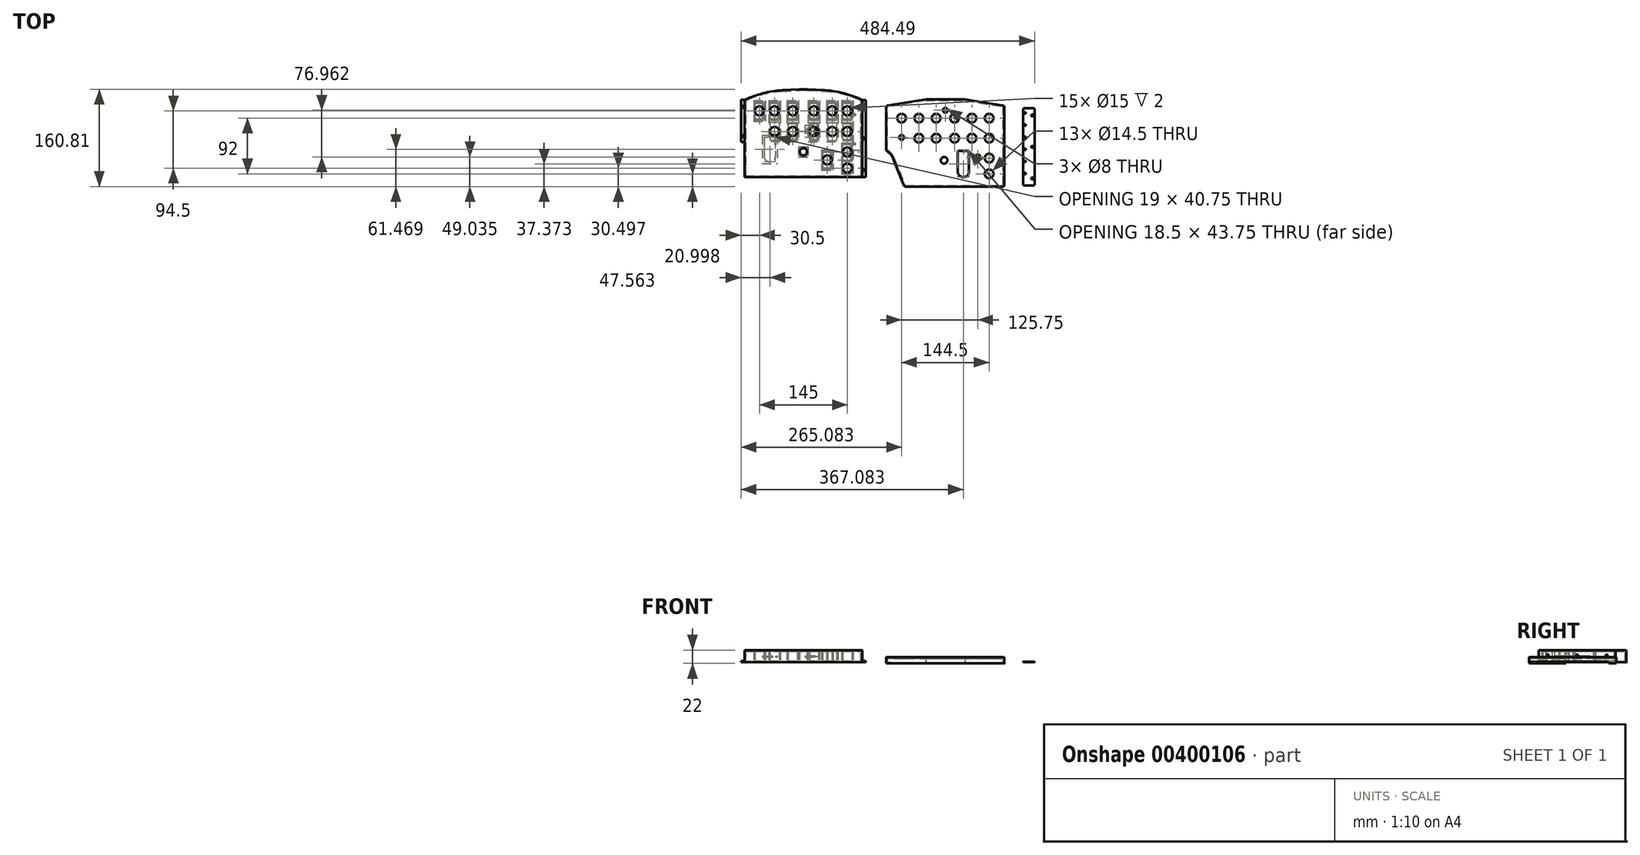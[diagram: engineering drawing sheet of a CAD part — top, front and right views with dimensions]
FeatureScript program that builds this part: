
annotation { "Feature Type Name" : "Feature", "Feature Type Description" : "" }
export const myFeature = defineFeature(function(context is Context, id is Id, definition is map)
    precondition{}
    {
        {
            var Q0;
            Q0=qCreatedBy(makeId("Top.planeOp"),FACE);
            var sketch = newSketch(context, id + "F0", { "sketchPlane" : qUnion([Q0])});
            skLineSegment(sketch, "E0.bottom", {"start": v(-74, 30.66) * mm, "end": v(-59, 30.66) * mm});
            skLineSegment(sketch, "E0.top", {"start": v(-74, 0.66) * mm, "end": v(-59, 0.66) * mm});
            skLineSegment(sketch, "E0.left", {"start": v(-74, 30.66) * mm, "end": v(-74, 0.66) * mm});
            skLineSegment(sketch, "E0.right", {"start": v(-59, 30.66) * mm, "end": v(-59, 0.66) * mm});
            skLineSegment(sketch, "E1.bottom", {"start": v(-49, 30.66) * mm, "end": v(-34, 30.66) * mm});
            skLineSegment(sketch, "E1.top", {"start": v(-49, 0.66) * mm, "end": v(-34, 0.66) * mm});
            skLineSegment(sketch, "E1.left", {"start": v(-49, 30.66) * mm, "end": v(-49, 0.66) * mm});
            skLineSegment(sketch, "E1.right", {"start": v(-34, 30.66) * mm, "end": v(-34, 0.66) * mm});
            skLineSegment(sketch, "E2.bottom", {"start": v(-19, 30.66) * mm, "end": v(-4, 30.66) * mm});
            skLineSegment(sketch, "E2.top", {"start": v(-19, 0.66) * mm, "end": v(-4, 0.66) * mm});
            skLineSegment(sketch, "E2.left", {"start": v(-19, 30.66) * mm, "end": v(-19, 0.66) * mm});
            skLineSegment(sketch, "E2.right", {"start": v(-4, 30.66) * mm, "end": v(-4, 0.66) * mm});
            skLineSegment(sketch, "E3.bottom", {"start": v(16, 30.66) * mm, "end": v(31, 30.66) * mm});
            skLineSegment(sketch, "E3.top", {"start": v(16, 0.66) * mm, "end": v(31, 0.66) * mm});
            skLineSegment(sketch, "E3.left", {"start": v(16, 30.66) * mm, "end": v(16, 0.66) * mm});
            skLineSegment(sketch, "E3.right", {"start": v(31, 30.66) * mm, "end": v(31, 0.66) * mm});
            skLineSegment(sketch, "E4.bottom", {"start": v(46, 30.66) * mm, "end": v(61, 30.66) * mm});
            skLineSegment(sketch, "E4.top", {"start": v(46, 0.66) * mm, "end": v(61, 0.66) * mm});
            skLineSegment(sketch, "E4.left", {"start": v(46, 30.66) * mm, "end": v(46, 0.66) * mm});
            skLineSegment(sketch, "E4.right", {"start": v(61, 30.66) * mm, "end": v(61, 0.66) * mm});
            skLineSegment(sketch, "E5.bottom", {"start": v(71, 30.66) * mm, "end": v(86, 30.66) * mm});
            skLineSegment(sketch, "E5.top", {"start": v(71, 0.66) * mm, "end": v(86, 0.66) * mm});
            skLineSegment(sketch, "E5.left", {"start": v(71, 30.66) * mm, "end": v(71, 0.66) * mm});
            skLineSegment(sketch, "E5.right", {"start": v(86, 30.66) * mm, "end": v(86, 0.66) * mm});
            skLineSegment(sketch, "E6.bottom", {"start": v(-19, -3.34) * mm, "end": v(-4, -3.34) * mm});
            skLineSegment(sketch, "E6.top", {"start": v(-19, -33.34) * mm, "end": v(-4, -33.34) * mm});
            skLineSegment(sketch, "E6.left", {"start": v(-19, -3.34) * mm, "end": v(-19, -33.34) * mm});
            skLineSegment(sketch, "E6.right", {"start": v(-4, -3.34) * mm, "end": v(-4, -33.34) * mm});
            skLineSegment(sketch, "E7.bottom", {"start": v(16, -3.34) * mm, "end": v(31, -3.34) * mm});
            skLineSegment(sketch, "E7.top", {"start": v(16, -33.34) * mm, "end": v(31, -33.34) * mm});
            skLineSegment(sketch, "E7.left", {"start": v(16, -3.34) * mm, "end": v(16, -33.34) * mm});
            skLineSegment(sketch, "E7.right", {"start": v(31, -3.34) * mm, "end": v(31, -33.34) * mm});
            skLineSegment(sketch, "E8.bottom", {"start": v(46, -3.34) * mm, "end": v(61, -3.34) * mm});
            skLineSegment(sketch, "E8.top", {"start": v(46, -33.34) * mm, "end": v(61, -33.34) * mm});
            skLineSegment(sketch, "E8.left", {"start": v(46, -3.34) * mm, "end": v(46, -33.34) * mm});
            skLineSegment(sketch, "E8.right", {"start": v(61, -3.34) * mm, "end": v(61, -33.34) * mm});
            skLineSegment(sketch, "E9.bottom", {"start": v(71, -3.34) * mm, "end": v(86, -3.34) * mm});
            skLineSegment(sketch, "E9.top", {"start": v(71, -33.34) * mm, "end": v(86, -33.34) * mm});
            skLineSegment(sketch, "E9.left", {"start": v(71, -3.34) * mm, "end": v(71, -33.34) * mm});
            skLineSegment(sketch, "E9.right", {"start": v(86, -3.34) * mm, "end": v(86, -33.34) * mm});
            skLineSegment(sketch, "E10.bottom", {"start": v(71, -37.34) * mm, "end": v(86, -37.34) * mm});
            skLineSegment(sketch, "E10.top", {"start": v(71, -67.34) * mm, "end": v(86, -67.34) * mm});
            skLineSegment(sketch, "E10.left", {"start": v(71, -37.34) * mm, "end": v(71, -67.34) * mm});
            skLineSegment(sketch, "E10.right", {"start": v(86, -37.34) * mm, "end": v(86, -67.34) * mm});
            skLineSegment(sketch, "E11.bottom", {"start": v(-34, -3.34) * mm, "end": v(-49, -3.34) * mm});
            skLineSegment(sketch, "E11.top", {"start": v(-34, -33.34) * mm, "end": v(-49, -33.34) * mm});
            skLineSegment(sketch, "E11.left", {"start": v(-34, -3.34) * mm, "end": v(-34, -33.34) * mm});
            skLineSegment(sketch, "E11.right", {"start": v(-49, -3.34) * mm, "end": v(-49, -33.34) * mm});
            skLineSegment(sketch, "E12.bottom", {"start": v(0, -45.34) * mm, "end": v(12, -45.34) * mm});
            skLineSegment(sketch, "E12.top", {"start": v(0, -58.34) * mm, "end": v(12, -58.34) * mm});
            skLineSegment(sketch, "E12.left", {"start": v(0, -45.34) * mm, "end": v(0, -58.34) * mm});
            skLineSegment(sketch, "E12.right", {"start": v(12, -45.34) * mm, "end": v(12, -58.34) * mm});
            skLineSegment(sketch, "E13.bottom", {"start": v(38, -50.34) * mm, "end": v(53, -50.34) * mm});
            skLineSegment(sketch, "E13.top", {"start": v(38, -80.34) * mm, "end": v(53, -80.34) * mm});
            skLineSegment(sketch, "E13.left", {"start": v(38, -50.34) * mm, "end": v(38, -80.34) * mm});
            skLineSegment(sketch, "E13.right", {"start": v(53, -50.34) * mm, "end": v(53, -80.34) * mm});
            skLineSegment(sketch, "E14.bottom", {"start": v(71, -71.34) * mm, "end": v(86, -71.34) * mm});
            skLineSegment(sketch, "E14.top", {"start": v(71, -86.34) * mm, "end": v(86, -86.34) * mm});
            skLineSegment(sketch, "E14.left", {"start": v(71, -71.34) * mm, "end": v(71, -86.34) * mm});
            skLineSegment(sketch, "E14.right", {"start": v(86, -71.34) * mm, "end": v(86, -86.34) * mm});
            skLineSegment(sketch, "E15.bottom", {"start": v(-89, 33.66) * mm, "end": v(101, 33.66) * mm});
            skLineSegment(sketch, "E15.top", {"start": v(-89, -91.34) * mm, "end": v(101, -91.34) * mm});
            skLineSegment(sketch, "E15.left", {"start": v(-89, 33.66) * mm, "end": v(-89, -91.34) * mm});
            skLineSegment(sketch, "E15.right", {"start": v(101, 33.66) * mm, "end": v(101, -91.34) * mm});
            skSolve(sketch);
        }
        {
            var Q0;
            Q0=makeQuery(id+"F0.imprint","IMPRINT",FACE,{"disambiguationData":[TD([[makeQuery(id+"F0.imprint","IMPRINT",EDGE,{"derivedFrom":sQuery(id+"F0.wireOp",EDGE,"E0.bottom")}),1.0]])]});
            extrude(context, id + "F1", {"entities" : qUnion([Q0]), "depth" : 18 * mm});
        }
        {
            var Q0;
            Q0=makeQuery(id+"F1.opExtrude","CAP_FACE",FACE,{"disambiguationData":[OSD([sQuery(id+"F0.wireOp",EDGE,"E0.bottom"),sQuery(id+"F0.wireOp",EDGE,"E0.top"),sQuery(id+"F0.wireOp",EDGE,"E0.left"),sQuery(id+"F0.wireOp",EDGE,"E0.right"),sQuery(id+"F0.wireOp",EDGE,"E1.bottom"),sQuery(id+"F0.wireOp",EDGE,"E1.top"),sQuery(id+"F0.wireOp",EDGE,"E1.left"),sQuery(id+"F0.wireOp",EDGE,"E1.right"),sQuery(id+"F0.wireOp",EDGE,"E2.bottom"),sQuery(id+"F0.wireOp",EDGE,"E2.top"),sQuery(id+"F0.wireOp",EDGE,"E2.left"),sQuery(id+"F0.wireOp",EDGE,"E2.right"),sQuery(id+"F0.wireOp",EDGE,"E3.bottom"),sQuery(id+"F0.wireOp",EDGE,"E3.top"),sQuery(id+"F0.wireOp",EDGE,"E3.left"),sQuery(id+"F0.wireOp",EDGE,"E3.right"),sQuery(id+"F0.wireOp",EDGE,"E4.bottom"),sQuery(id+"F0.wireOp",EDGE,"E4.top"),sQuery(id+"F0.wireOp",EDGE,"E4.left"),sQuery(id+"F0.wireOp",EDGE,"E4.right"),sQuery(id+"F0.wireOp",EDGE,"E5.bottom"),sQuery(id+"F0.wireOp",EDGE,"E5.top"),sQuery(id+"F0.wireOp",EDGE,"E5.left"),sQuery(id+"F0.wireOp",EDGE,"E5.right"),sQuery(id+"F0.wireOp",EDGE,"E6.bottom"),sQuery(id+"F0.wireOp",EDGE,"E6.top"),sQuery(id+"F0.wireOp",EDGE,"E6.left"),sQuery(id+"F0.wireOp",EDGE,"E6.right"),sQuery(id+"F0.wireOp",EDGE,"E7.bottom"),sQuery(id+"F0.wireOp",EDGE,"E7.top"),sQuery(id+"F0.wireOp",EDGE,"E7.left"),sQuery(id+"F0.wireOp",EDGE,"E7.right"),sQuery(id+"F0.wireOp",EDGE,"E8.bottom"),sQuery(id+"F0.wireOp",EDGE,"E8.top"),sQuery(id+"F0.wireOp",EDGE,"E8.left"),sQuery(id+"F0.wireOp",EDGE,"E8.right"),sQuery(id+"F0.wireOp",EDGE,"E9.bottom"),sQuery(id+"F0.wireOp",EDGE,"E9.top"),sQuery(id+"F0.wireOp",EDGE,"E9.left"),sQuery(id+"F0.wireOp",EDGE,"E9.right"),sQuery(id+"F0.wireOp",EDGE,"E10.bottom"),sQuery(id+"F0.wireOp",EDGE,"E10.top"),sQuery(id+"F0.wireOp",EDGE,"E10.left"),sQuery(id+"F0.wireOp",EDGE,"E10.right"),sQuery(id+"F0.wireOp",EDGE,"E11.bottom"),sQuery(id+"F0.wireOp",EDGE,"E11.top"),sQuery(id+"F0.wireOp",EDGE,"E11.left"),sQuery(id+"F0.wireOp",EDGE,"E11.right"),sQuery(id+"F0.wireOp",EDGE,"E12.bottom"),sQuery(id+"F0.wireOp",EDGE,"E12.top"),sQuery(id+"F0.wireOp",EDGE,"E12.left"),sQuery(id+"F0.wireOp",EDGE,"E12.right"),sQuery(id+"F0.wireOp",EDGE,"E13.bottom"),sQuery(id+"F0.wireOp",EDGE,"E13.top"),sQuery(id+"F0.wireOp",EDGE,"E13.left"),sQuery(id+"F0.wireOp",EDGE,"E13.right"),sQuery(id+"F0.wireOp",EDGE,"E14.bottom"),sQuery(id+"F0.wireOp",EDGE,"E14.top"),sQuery(id+"F0.wireOp",EDGE,"E14.left"),sQuery(id+"F0.wireOp",EDGE,"E14.right"),sQuery(id+"F0.wireOp",EDGE,"E15.bottom"),sQuery(id+"F0.wireOp",EDGE,"E15.top"),sQuery(id+"F0.wireOp",EDGE,"E15.left"),sQuery(id+"F0.wireOp",EDGE,"E15.right")])],"isStart":false});
            var sketch = newSketch(context, id + "F2", { "sketchPlane" : qUnion([Q0])});
            skLineSegment(sketch, "E16.bottom", {"start": v(-89, 33.66) * mm, "end": v(101, 33.66) * mm});
            skLineSegment(sketch, "E16.top", {"start": v(-89, -91.34) * mm, "end": v(101, -91.34) * mm});
            skLineSegment(sketch, "E16.left", {"start": v(-89, 33.66) * mm, "end": v(-89, -91.34) * mm});
            skLineSegment(sketch, "E16.right", {"start": v(101, 33.66) * mm, "end": v(101, -91.34) * mm});
            skCircle(sketch, "E17", {"center": v(-66.5, 15.66) * mm, "radius": 7.5 * mm});
            skPoint(sketch, "E18", {"position": v(-66.5, 30.66) * mm});
            skCircle(sketch, "E19", {"center": v(-41.5, 15.66) * mm, "radius": 7.5 * mm});
            skPoint(sketch, "E19.centerSnap0", {"position": v(-41.5, 30.66) * mm});
            skCircle(sketch, "E20", {"center": v(-11.5, 15.66) * mm, "radius": 7.5 * mm});
            skPoint(sketch, "E20.centerSnap0", {"position": v(-11.5, 30.66) * mm});
            skPoint(sketch, "E20.centerSnap1", {"position": v(-34, 15.66) * mm});
            skCircle(sketch, "E21", {"center": v(23.5, 15.66) * mm, "radius": 7.5 * mm});
            skPoint(sketch, "E21.centerSnap0", {"position": v(23.5, 30.66) * mm});
            skCircle(sketch, "E22", {"center": v(53.5, 15.66) * mm, "radius": 7.5 * mm});
            skPoint(sketch, "E22.centerSnap0", {"position": v(53.5, 30.66) * mm});
            skPoint(sketch, "E22.centerSnap1", {"position": v(31, 15.66) * mm});
            skCircle(sketch, "E23", {"center": v(78.5, 15.66) * mm, "radius": 7.5 * mm});
            skPoint(sketch, "E23.centerSnap0", {"position": v(78.5, 30.66) * mm});
            skCircle(sketch, "E24", {"center": v(-11.5, -18.34) * mm, "radius": 7.5 * mm});
            skCircle(sketch, "E25", {"center": v(23.5, -18.34) * mm, "radius": 7.5 * mm});
            skPoint(sketch, "E25.centerSnap0", {"position": v(23.5, -3.34) * mm});
            skPoint(sketch, "E25.centerSnap1", {"position": v(-4, -18.34) * mm});
            skCircle(sketch, "E26", {"center": v(53.5, -18.34) * mm, "radius": 7.5 * mm});
            skPoint(sketch, "E26.centerSnap0", {"position": v(53.5, -3.34) * mm});
            skPoint(sketch, "E26.centerSnap1", {"position": v(31, -18.34) * mm});
            skCircle(sketch, "E27", {"center": v(78.5, -18.34) * mm, "radius": 7.5 * mm});
            skPoint(sketch, "E27.centerSnap0", {"position": v(78.5, -3.34) * mm});
            skCircle(sketch, "E28", {"center": v(45.5, -65.34) * mm, "radius": 7.5 * mm});
            skPoint(sketch, "E28.centerSnap0", {"position": v(45.5, -50.34) * mm});
            skCircle(sketch, "E29", {"center": v(78.5, -52.34) * mm, "radius": 7.5 * mm});
            skPoint(sketch, "E29.centerSnap0", {"position": v(78.5, -37.34) * mm});
            skCircle(sketch, "E30", {"center": v(-41.5, -18.34) * mm, "radius": 7.5 * mm});
            skPoint(sketch, "E30.centerSnap0", {"position": v(-41.5, -3.34) * mm});
            skCircle(sketch, "E31", {"center": v(78.5, -78.84) * mm, "radius": 7.5 * mm});
            skPoint(sketch, "E31.centerSnap0", {"position": v(86, -78.84) * mm});
            skCircle(sketch, "E32", {"center": v(6, -51.84) * mm, "radius": 6 * mm});
            skPoint(sketch, "E32.centerSnap0", {"position": v(0, -51.84) * mm});
            skPoint(sketch, "E32.centerSnap1", {"position": v(6, -45.34) * mm});
            skSolve(sketch);
        }
        {
            var Q0;
            Q0=qSketchRegion(id+"F2",true);
            extrude(context, id + "F3", {"entities" : qUnion([Q0]), "depth" : 2 * mm});
        }
        {
            var Q0;
            Q0=makeQuery(id+"F3.opExtrude","CAP_FACE",FACE,{"disambiguationData":[OSD([sQuery(id+"F2.wireOp",EDGE,"E16.bottom"),sQuery(id+"F2.wireOp",EDGE,"E16.top"),sQuery(id+"F2.wireOp",EDGE,"E16.left"),sQuery(id+"F2.wireOp",EDGE,"E16.right"),sQuery(id+"F2.wireOp",EDGE,"E17"),sQuery(id+"F2.wireOp",EDGE,"E19"),sQuery(id+"F2.wireOp",EDGE,"E20"),sQuery(id+"F2.wireOp",EDGE,"E21"),sQuery(id+"F2.wireOp",EDGE,"E22"),sQuery(id+"F2.wireOp",EDGE,"E23"),sQuery(id+"F2.wireOp",EDGE,"E24"),sQuery(id+"F2.wireOp",EDGE,"E25"),sQuery(id+"F2.wireOp",EDGE,"E26"),sQuery(id+"F2.wireOp",EDGE,"E27"),sQuery(id+"F2.wireOp",EDGE,"E28"),sQuery(id+"F2.wireOp",EDGE,"E29"),sQuery(id+"F2.wireOp",EDGE,"E30"),sQuery(id+"F2.wireOp",EDGE,"E31"),sQuery(id+"F2.wireOp",EDGE,"E32")])],"isStart":false});
            var sketch = newSketch(context, id + "F4", { "sketchPlane" : qUnion([Q0])});
            skLineSegment(sketch, "E33.bottom", {"start": v(-89, 33.66) * mm, "end": v(-91, 33.66) * mm});
            skLineSegment(sketch, "E33.top", {"start": v(-89, -91.34) * mm, "end": v(-91, -91.34) * mm});
            skLineSegment(sketch, "E33.left", {"start": v(-89, 33.66) * mm, "end": v(-89, -91.34) * mm});
            skLineSegment(sketch, "E33.right", {"start": v(-91, 33.66) * mm, "end": v(-91, -91.34) * mm});
            skLineSegment(sketch, "E34.bottom", {"start": v(101, 33.66) * mm, "end": v(103, 33.66) * mm});
            skLineSegment(sketch, "E34.top", {"start": v(101, -91.34) * mm, "end": v(103, -91.34) * mm});
            skLineSegment(sketch, "E34.left", {"start": v(101, 33.66) * mm, "end": v(101, -91.34) * mm});
            skLineSegment(sketch, "E34.right", {"start": v(103, 33.66) * mm, "end": v(103, -91.34) * mm});
            skLineSegment(sketch, "E35.bottom", {"start": v(-91, -91.34) * mm, "end": v(103, -91.34) * mm});
            skLineSegment(sketch, "E35.top", {"start": v(-91, -93.34) * mm, "end": v(103, -93.34) * mm});
            skLineSegment(sketch, "E35.left", {"start": v(-91, -91.34) * mm, "end": v(-91, -93.34) * mm});
            skLineSegment(sketch, "E35.right", {"start": v(103, -91.34) * mm, "end": v(103, -93.34) * mm});
            skLineSegment(sketch, "E36", {"start": v(-29, 49.65) * mm, "end": v(-29, 33.66) * mm});
            skLineSegment(sketch, "E37", {"start": v(41, 49.65) * mm, "end": v(41, 33.66) * mm});
            skPoint(sketch, "E38.orphan", {"position": v(103, 49.4) * mm});
            skLineSegment(sketch, "E39", {"start": v(-29, 49.65) * mm, "end": v(6, 51.66) * mm});
            skLineSegment(sketch, "E40", {"start": v(6, 51.66) * mm, "end": v(41, 49.65) * mm});
            skArc(sketch, "E41", {"start": v(-29, 49.65) * mm, "mid": v(-60.78, 44.7) * mm, "end": v(-91, 33.66) * mm});
            skArc(sketch, "E42", {"start": v(103, 33.66) * mm, "mid": v(72.78, 44.7) * mm, "end": v(41, 49.65) * mm});
            skLineSegment(sketch, "E43.bottom", {"start": v(-89, 33.66) * mm, "end": v(101, 33.66) * mm});
            skLineSegment(sketch, "E43.top", {"start": v(-89, -91.34) * mm, "end": v(101, -91.34) * mm});
            skSolve(sketch);
        }
        {
            var Q0;
            Q0=qSketchRegion(id+"F4",true);
            extrude(context, id + "F5", {"entities" : qUnion([Q0]), "operationType" : NewBodyOperationType.ADD, "oppositeDirection" : true, "depth" : 20 * mm});
        }
        {
            var Q0;
            Q0=makeQuery(id+"F5.opExtrude","SWEPT_EDGE",EDGE,{"disambiguationData":[OSD([sQuery(id+"F4.wireOp",EDGE,"E39"),sQuery(id+"F4.wireOp",EDGE,"E40")])]});
            fillet(context, id + "F6", {"entities" : qUnion([Q0]), "radius" : 115.17 * mm, "tangentPropagation" : true, "allowEdgeOverflow" : false});
        }
        {
            var Q0;
            Q0=makeQuery(id+"F5.opExtrude","CAP_FACE",FACE,{"disambiguationData":[OSD([sQuery(id+"F4.wireOp",EDGE,"E33.right"),sQuery(id+"F4.wireOp",EDGE,"E34.right"),sQuery(id+"F4.wireOp",EDGE,"E35.top"),sQuery(id+"F4.wireOp",EDGE,"E35.left"),sQuery(id+"F4.wireOp",EDGE,"E35.right"),sQuery(id+"F4.wireOp",EDGE,"E39"),sQuery(id+"F4.wireOp",EDGE,"E40"),sQuery(id+"F4.wireOp",EDGE,"E41"),sQuery(id+"F4.wireOp",EDGE,"E42")])],"isStart":false});
            shell(context, id + "F7", {"entities" : qUnion([Q0]), "thickness" : 2 * mm});
        }
        {
            var Q0;
            Q0=makeQuery(id+"F1.opExtrude","CAP_FACE",FACE,{"disambiguationData":[OSD([sQuery(id+"F0.wireOp",EDGE,"E0.bottom"),sQuery(id+"F0.wireOp",EDGE,"E0.top"),sQuery(id+"F0.wireOp",EDGE,"E0.left"),sQuery(id+"F0.wireOp",EDGE,"E0.right"),sQuery(id+"F0.wireOp",EDGE,"E1.bottom"),sQuery(id+"F0.wireOp",EDGE,"E1.top"),sQuery(id+"F0.wireOp",EDGE,"E1.left"),sQuery(id+"F0.wireOp",EDGE,"E1.right"),sQuery(id+"F0.wireOp",EDGE,"E2.bottom"),sQuery(id+"F0.wireOp",EDGE,"E2.top"),sQuery(id+"F0.wireOp",EDGE,"E2.left"),sQuery(id+"F0.wireOp",EDGE,"E2.right"),sQuery(id+"F0.wireOp",EDGE,"E3.bottom"),sQuery(id+"F0.wireOp",EDGE,"E3.top"),sQuery(id+"F0.wireOp",EDGE,"E3.left"),sQuery(id+"F0.wireOp",EDGE,"E3.right"),sQuery(id+"F0.wireOp",EDGE,"E4.bottom"),sQuery(id+"F0.wireOp",EDGE,"E4.top"),sQuery(id+"F0.wireOp",EDGE,"E4.left"),sQuery(id+"F0.wireOp",EDGE,"E4.right"),sQuery(id+"F0.wireOp",EDGE,"E5.bottom"),sQuery(id+"F0.wireOp",EDGE,"E5.top"),sQuery(id+"F0.wireOp",EDGE,"E5.left"),sQuery(id+"F0.wireOp",EDGE,"E5.right"),sQuery(id+"F0.wireOp",EDGE,"E6.bottom"),sQuery(id+"F0.wireOp",EDGE,"E6.top"),sQuery(id+"F0.wireOp",EDGE,"E6.left"),sQuery(id+"F0.wireOp",EDGE,"E6.right"),sQuery(id+"F0.wireOp",EDGE,"E7.bottom"),sQuery(id+"F0.wireOp",EDGE,"E7.top"),sQuery(id+"F0.wireOp",EDGE,"E7.left"),sQuery(id+"F0.wireOp",EDGE,"E7.right"),sQuery(id+"F0.wireOp",EDGE,"E8.bottom"),sQuery(id+"F0.wireOp",EDGE,"E8.top"),sQuery(id+"F0.wireOp",EDGE,"E8.left"),sQuery(id+"F0.wireOp",EDGE,"E8.right"),sQuery(id+"F0.wireOp",EDGE,"E9.bottom"),sQuery(id+"F0.wireOp",EDGE,"E9.top"),sQuery(id+"F0.wireOp",EDGE,"E9.left"),sQuery(id+"F0.wireOp",EDGE,"E9.right"),sQuery(id+"F0.wireOp",EDGE,"E10.bottom"),sQuery(id+"F0.wireOp",EDGE,"E10.top"),sQuery(id+"F0.wireOp",EDGE,"E10.left"),sQuery(id+"F0.wireOp",EDGE,"E10.right"),sQuery(id+"F0.wireOp",EDGE,"E11.bottom"),sQuery(id+"F0.wireOp",EDGE,"E11.top"),sQuery(id+"F0.wireOp",EDGE,"E11.left"),sQuery(id+"F0.wireOp",EDGE,"E11.right"),sQuery(id+"F0.wireOp",EDGE,"E12.bottom"),sQuery(id+"F0.wireOp",EDGE,"E12.top"),sQuery(id+"F0.wireOp",EDGE,"E12.left"),sQuery(id+"F0.wireOp",EDGE,"E12.right"),sQuery(id+"F0.wireOp",EDGE,"E13.bottom"),sQuery(id+"F0.wireOp",EDGE,"E13.top"),sQuery(id+"F0.wireOp",EDGE,"E13.left"),sQuery(id+"F0.wireOp",EDGE,"E13.right"),sQuery(id+"F0.wireOp",EDGE,"E14.bottom"),sQuery(id+"F0.wireOp",EDGE,"E14.top"),sQuery(id+"F0.wireOp",EDGE,"E14.left"),sQuery(id+"F0.wireOp",EDGE,"E14.right"),sQuery(id+"F0.wireOp",EDGE,"E15.bottom"),sQuery(id+"F0.wireOp",EDGE,"E15.top"),sQuery(id+"F0.wireOp",EDGE,"E15.left"),sQuery(id+"F0.wireOp",EDGE,"E15.right")])],"isStart":true});
            var sketch = newSketch(context, id + "F8", { "sketchPlane" : qUnion([Q0])});
            skLineSegment(sketch, "E44.bottom", {"start": v(-97, -34.16) * mm, "end": v(-91, -34.16) * mm});
            skLineSegment(sketch, "E44.top", {"start": v(-97, 35.84) * mm, "end": v(-91, 35.84) * mm});
            skLineSegment(sketch, "E44.left", {"start": v(-97, -34.16) * mm, "end": v(-97, 35.84) * mm});
            skLineSegment(sketch, "E44.right", {"start": v(-91, -34.16) * mm, "end": v(-91, 35.84) * mm});
            skLineSegment(sketch, "E45.bottom", {"start": v(103, -33.66) * mm, "end": v(109, -33.66) * mm});
            skLineSegment(sketch, "E45.top", {"start": v(103, 93.34) * mm, "end": v(109, 93.34) * mm});
            skLineSegment(sketch, "E45.left", {"start": v(103, -33.66) * mm, "end": v(103, 93.34) * mm});
            skLineSegment(sketch, "E45.right", {"start": v(109, -33.66) * mm, "end": v(109, 93.34) * mm});
            skCircle(sketch, "E46", {"center": v(-94, -22.16) * mm, "radius": 1.5 * mm});
            skCircle(sketch, "E47", {"center": v(-94, 25.84) * mm, "radius": 1.5 * mm});
            skCircle(sketch, "E48", {"center": v(106, -22.16) * mm, "radius": 1.5 * mm});
            skCircle(sketch, "E49", {"center": v(106, 29.84) * mm, "radius": 1.5 * mm});
            skCircle(sketch, "E50", {"center": v(106, 81.84) * mm, "radius": 1.5 * mm});
            skSolve(sketch);
        }
        {
            var Q0;
            Q0=qSketchRegion(id+"F8",true);
            extrude(context, id + "F9", {"entities" : qUnion([Q0]), "operationType" : NewBodyOperationType.ADD, "oppositeDirection" : true, "depth" : 2 * mm});
        }
        {
            var Q0;
            Q0=makeQuery(id+"F5.opExtrude","SWEPT_FACE",FACE,{"disambiguationData":[OSD([sQuery(id+"F4.wireOp",EDGE,"E33.right"),sQuery(id+"F4.wireOp",EDGE,"E35.left")])]});
            var sketch = newSketch(context, id + "F10", { "sketchPlane" : qUnion([Q0])});
            skCircle(sketch, "E51", {"center": v(-18.66, 11) * mm, "radius": 1.5 * mm});
            skCircle(sketch, "E52", {"center": v(78.38, 11) * mm, "radius": 1.5 * mm});
            skCircle(sketch, "E53", {"center": v(29.88, 11) * mm, "radius": 1.5 * mm});
            skSolve(sketch);
        }
        {
            var Q0;
            Q0=qSketchRegion(id+"F10",true);
            extrude(context, id + "F11", {"entities" : qUnion([Q0]), "operationType" : NewBodyOperationType.REMOVE, "oppositeDirection" : true, "depth" : 8 * mm});
        }
        {
            var Q0;
            Q0=makeQuery(id+"F5.opExtrude","SWEPT_FACE",FACE,{"disambiguationData":[OSD([sQuery(id+"F4.wireOp",EDGE,"E34.right"),sQuery(id+"F4.wireOp",EDGE,"E35.right")])]});
            var sketch = newSketch(context, id + "F12", { "sketchPlane" : qUnion([Q0])});
            skCircle(sketch, "E54", {"center": v(-78.34, 11) * mm, "radius": 1.5 * mm});
            skCircle(sketch, "E55", {"center": v(18.66, 11) * mm, "radius": 1.5 * mm});
            skCircle(sketch, "E56", {"center": v(-29.84, 11) * mm, "radius": 1.5 * mm});
            skSolve(sketch);
        }
        {
            var Q0;
            Q0=qSketchRegion(id+"F12",true);
            extrude(context, id + "F13", {"entities" : qUnion([Q0]), "operationType" : NewBodyOperationType.REMOVE, "oppositeDirection" : true, "depth" : 8 * mm});
        }
        {
            var Q0;
            Q0=makeQuery(id+"F1.opExtrude","CAP_FACE",FACE,{"disambiguationData":[OSD([sQuery(id+"F0.wireOp",EDGE,"E0.bottom"),sQuery(id+"F0.wireOp",EDGE,"E0.top"),sQuery(id+"F0.wireOp",EDGE,"E0.left"),sQuery(id+"F0.wireOp",EDGE,"E0.right"),sQuery(id+"F0.wireOp",EDGE,"E1.bottom"),sQuery(id+"F0.wireOp",EDGE,"E1.top"),sQuery(id+"F0.wireOp",EDGE,"E1.left"),sQuery(id+"F0.wireOp",EDGE,"E1.right"),sQuery(id+"F0.wireOp",EDGE,"E2.bottom"),sQuery(id+"F0.wireOp",EDGE,"E2.top"),sQuery(id+"F0.wireOp",EDGE,"E2.left"),sQuery(id+"F0.wireOp",EDGE,"E2.right"),sQuery(id+"F0.wireOp",EDGE,"E3.bottom"),sQuery(id+"F0.wireOp",EDGE,"E3.top"),sQuery(id+"F0.wireOp",EDGE,"E3.left"),sQuery(id+"F0.wireOp",EDGE,"E3.right"),sQuery(id+"F0.wireOp",EDGE,"E4.bottom"),sQuery(id+"F0.wireOp",EDGE,"E4.top"),sQuery(id+"F0.wireOp",EDGE,"E4.left"),sQuery(id+"F0.wireOp",EDGE,"E4.right"),sQuery(id+"F0.wireOp",EDGE,"E5.bottom"),sQuery(id+"F0.wireOp",EDGE,"E5.top"),sQuery(id+"F0.wireOp",EDGE,"E5.left"),sQuery(id+"F0.wireOp",EDGE,"E5.right"),sQuery(id+"F0.wireOp",EDGE,"E6.bottom"),sQuery(id+"F0.wireOp",EDGE,"E6.top"),sQuery(id+"F0.wireOp",EDGE,"E6.left"),sQuery(id+"F0.wireOp",EDGE,"E6.right"),sQuery(id+"F0.wireOp",EDGE,"E7.bottom"),sQuery(id+"F0.wireOp",EDGE,"E7.top"),sQuery(id+"F0.wireOp",EDGE,"E7.left"),sQuery(id+"F0.wireOp",EDGE,"E7.right"),sQuery(id+"F0.wireOp",EDGE,"E8.bottom"),sQuery(id+"F0.wireOp",EDGE,"E8.top"),sQuery(id+"F0.wireOp",EDGE,"E8.left"),sQuery(id+"F0.wireOp",EDGE,"E8.right"),sQuery(id+"F0.wireOp",EDGE,"E9.bottom"),sQuery(id+"F0.wireOp",EDGE,"E9.top"),sQuery(id+"F0.wireOp",EDGE,"E9.left"),sQuery(id+"F0.wireOp",EDGE,"E9.right"),sQuery(id+"F0.wireOp",EDGE,"E10.bottom"),sQuery(id+"F0.wireOp",EDGE,"E10.top"),sQuery(id+"F0.wireOp",EDGE,"E10.left"),sQuery(id+"F0.wireOp",EDGE,"E10.right"),sQuery(id+"F0.wireOp",EDGE,"E11.bottom"),sQuery(id+"F0.wireOp",EDGE,"E11.top"),sQuery(id+"F0.wireOp",EDGE,"E11.left"),sQuery(id+"F0.wireOp",EDGE,"E11.right"),sQuery(id+"F0.wireOp",EDGE,"E12.bottom"),sQuery(id+"F0.wireOp",EDGE,"E12.top"),sQuery(id+"F0.wireOp",EDGE,"E12.left"),sQuery(id+"F0.wireOp",EDGE,"E12.right"),sQuery(id+"F0.wireOp",EDGE,"E13.bottom"),sQuery(id+"F0.wireOp",EDGE,"E13.top"),sQuery(id+"F0.wireOp",EDGE,"E13.left"),sQuery(id+"F0.wireOp",EDGE,"E13.right"),sQuery(id+"F0.wireOp",EDGE,"E14.bottom"),sQuery(id+"F0.wireOp",EDGE,"E14.top"),sQuery(id+"F0.wireOp",EDGE,"E14.left"),sQuery(id+"F0.wireOp",EDGE,"E14.right"),sQuery(id+"F0.wireOp",EDGE,"E15.bottom"),sQuery(id+"F0.wireOp",EDGE,"E15.top"),sQuery(id+"F0.wireOp",EDGE,"E15.left"),sQuery(id+"F0.wireOp",EDGE,"E15.right")])],"isStart":true});
            var sketch = newSketch(context, id + "F14", { "sketchPlane" : qUnion([Q0])});
            skLineSegment(sketch, "E57.bottom", {"start": v(-19, -2.66) * mm, "end": v(-6, -2.66) * mm});
            skLineSegment(sketch, "E57.top", {"start": v(-19, -28.66) * mm, "end": v(-6, -28.66) * mm});
            skLineSegment(sketch, "E57.left", {"start": v(-19, -2.66) * mm, "end": v(-19, -28.66) * mm});
            skLineSegment(sketch, "E57.right", {"start": v(-6, -2.66) * mm, "end": v(-6, -28.66) * mm});
            skLineSegment(sketch, "E58.bottom", {"start": v(-49, -2.66) * mm, "end": v(-36, -2.66) * mm});
            skLineSegment(sketch, "E58.top", {"start": v(-49, -28.66) * mm, "end": v(-36, -28.66) * mm});
            skLineSegment(sketch, "E58.left", {"start": v(-49, -2.66) * mm, "end": v(-49, -28.66) * mm});
            skLineSegment(sketch, "E58.right", {"start": v(-36, -2.66) * mm, "end": v(-36, -28.66) * mm});
            skLineSegment(sketch, "E59.bottom", {"start": v(-74, -2.66) * mm, "end": v(-61, -2.66) * mm});
            skLineSegment(sketch, "E59.top", {"start": v(-74, -28.66) * mm, "end": v(-61, -28.66) * mm});
            skLineSegment(sketch, "E59.left", {"start": v(-74, -2.66) * mm, "end": v(-74, -28.66) * mm});
            skLineSegment(sketch, "E59.right", {"start": v(-61, -2.66) * mm, "end": v(-61, -28.66) * mm});
            skLineSegment(sketch, "E60.bottom", {"start": v(16, -2.66) * mm, "end": v(29, -2.66) * mm});
            skLineSegment(sketch, "E60.top", {"start": v(16, -28.66) * mm, "end": v(29, -28.66) * mm});
            skLineSegment(sketch, "E60.left", {"start": v(16, -2.66) * mm, "end": v(16, -28.66) * mm});
            skLineSegment(sketch, "E60.right", {"start": v(29, -2.66) * mm, "end": v(29, -28.66) * mm});
            skLineSegment(sketch, "E61.bottom", {"start": v(46, -2.66) * mm, "end": v(59, -2.66) * mm});
            skLineSegment(sketch, "E61.top", {"start": v(46, -28.66) * mm, "end": v(59, -28.66) * mm});
            skLineSegment(sketch, "E61.left", {"start": v(46, -2.66) * mm, "end": v(46, -28.66) * mm});
            skLineSegment(sketch, "E61.right", {"start": v(59, -2.66) * mm, "end": v(59, -28.66) * mm});
            skLineSegment(sketch, "E62.bottom", {"start": v(71, -2.66) * mm, "end": v(84, -2.66) * mm});
            skLineSegment(sketch, "E62.top", {"start": v(71, -28.66) * mm, "end": v(84, -28.66) * mm});
            skLineSegment(sketch, "E62.left", {"start": v(71, -2.66) * mm, "end": v(71, -28.66) * mm});
            skLineSegment(sketch, "E62.right", {"start": v(84, -2.66) * mm, "end": v(84, -28.66) * mm});
            skLineSegment(sketch, "E63.bottom", {"start": v(-19, 31.34) * mm, "end": v(-6, 31.34) * mm});
            skLineSegment(sketch, "E63.top", {"start": v(-19, 5.34) * mm, "end": v(-6, 5.34) * mm});
            skLineSegment(sketch, "E63.left", {"start": v(-19, 31.34) * mm, "end": v(-19, 5.34) * mm});
            skLineSegment(sketch, "E63.right", {"start": v(-6, 31.34) * mm, "end": v(-6, 5.34) * mm});
            skLineSegment(sketch, "E64.bottom", {"start": v(16, 31.34) * mm, "end": v(29, 31.34) * mm});
            skLineSegment(sketch, "E64.top", {"start": v(16, 5.34) * mm, "end": v(29, 5.34) * mm});
            skLineSegment(sketch, "E64.left", {"start": v(16, 31.34) * mm, "end": v(16, 5.34) * mm});
            skLineSegment(sketch, "E64.right", {"start": v(29, 31.34) * mm, "end": v(29, 5.34) * mm});
            skLineSegment(sketch, "E65.bottom", {"start": v(71, 31.34) * mm, "end": v(84, 31.34) * mm});
            skLineSegment(sketch, "E65.top", {"start": v(71, 5.34) * mm, "end": v(84, 5.34) * mm});
            skLineSegment(sketch, "E65.left", {"start": v(71, 31.34) * mm, "end": v(71, 5.34) * mm});
            skLineSegment(sketch, "E65.right", {"start": v(84, 31.34) * mm, "end": v(84, 5.34) * mm});
            skLineSegment(sketch, "E66.bottom", {"start": v(38, 78.34) * mm, "end": v(51, 78.34) * mm});
            skLineSegment(sketch, "E66.top", {"start": v(38, 52.34) * mm, "end": v(51, 52.34) * mm});
            skLineSegment(sketch, "E66.left", {"start": v(38, 78.34) * mm, "end": v(38, 52.34) * mm});
            skLineSegment(sketch, "E66.right", {"start": v(51, 78.34) * mm, "end": v(51, 52.34) * mm});
            skLineSegment(sketch, "E67.bottom", {"start": v(71, 65.34) * mm, "end": v(84, 65.34) * mm});
            skLineSegment(sketch, "E67.top", {"start": v(71, 39.34) * mm, "end": v(84, 39.34) * mm});
            skLineSegment(sketch, "E67.left", {"start": v(71, 65.34) * mm, "end": v(71, 39.34) * mm});
            skLineSegment(sketch, "E67.right", {"start": v(84, 65.34) * mm, "end": v(84, 39.34) * mm});
            skSolve(sketch);
        }
        {
            var Q0;
            Q0=qSketchRegion(id+"F14",true);
            extrude(context, id + "F15", {"entities" : qUnion([Q0]), "operationType" : NewBodyOperationType.ADD, "oppositeDirection" : true, "depth" : 2 * mm});
        }
        {
            var Q0;
            Q0=qCreatedBy(makeId("Top.planeOp"),FACE);
            var sketch = newSketch(context, id + "F16", { "sketchPlane" : qUnion([Q0])});
            skLineSegment(sketch, "E68.top", {"start": v(174.83, -109.34) * mm, "end": v(334.83, -109.34) * mm});
            skLineSegment(sketch, "E68.left", {"start": v(142.83, 21.7) * mm, "end": v(142.83, -48.58) * mm});
            skLineSegment(sketch, "E68.right", {"start": v(337.83, 21.7) * mm, "end": v(337.83, -106.34) * mm});
            skLineSegment(sketch, "E69", {"start": v(154.24, -63.04) * mm, "end": v(172.05, -107.46) * mm});
            skLineSegment(sketch, "E70", {"start": v(207.83, 34.66) * mm, "end": v(272.83, 34.66) * mm});
            skLineSegment(sketch, "E71", {"start": v(272.83, 34.66) * mm, "end": v(335.3, 24.66) * mm});
            skLineSegment(sketch, "E72", {"start": v(207.83, 34.66) * mm, "end": v(145.36, 24.66) * mm});
            skPoint(sketch, "E73.visualSharp", {"position": v(142.83, 24.25) * mm});
            skArc(sketch, "E73.filletArc", {"start": v(145.36, 24.66) * mm, "mid": v(143.55, 23.64) * mm, "end": v(142.83, 21.7) * mm});
            skPoint(sketch, "E74.visualSharp", {"position": v(337.83, 24.25) * mm});
            skArc(sketch, "E74.filletArc", {"start": v(337.83, 21.7) * mm, "mid": v(337.12, 23.64) * mm, "end": v(335.3, 24.66) * mm});
            skPoint(sketch, "E75.visualSharp", {"position": v(337.83, -109.34) * mm});
            skArc(sketch, "E75.filletArc", {"start": v(334.83, -109.34) * mm, "mid": v(336.95, -108.46) * mm, "end": v(337.83, -106.34) * mm});
            skPoint(sketch, "E76.visualSharp", {"position": v(172.8, -109.34) * mm});
            skArc(sketch, "E76.filletArc", {"start": v(172.05, -107.46) * mm, "mid": v(173.15, -108.83) * mm, "end": v(174.83, -109.34) * mm});
            skArc(sketch, "E77", {"start": v(154.24, -63.04) * mm, "mid": v(150.2, -56.29) * mm, "end": v(144.25, -51.12) * mm});
            skPoint(sketch, "E78.visualSharp", {"position": v(142.83, -50.3) * mm});
            skArc(sketch, "E78.filletArc", {"start": v(142.83, -48.58) * mm, "mid": v(143.2, -50.03) * mm, "end": v(144.25, -51.12) * mm});
            skSolve(sketch);
        }
        {
            var Q0;
            Q0=qSketchRegion(id+"F16",true);
            extrude(context, id + "F17", {"entities" : qUnion([Q0]), "depth" : 8 * mm});
        }
        {
            var Q0;
            Q0=makeQuery(id+"F17.opExtrude","CAP_FACE",FACE,{"disambiguationData":[OSD([sQuery(id+"F16.wireOp",EDGE,"E68.top"),sQuery(id+"F16.wireOp",EDGE,"E68.left"),sQuery(id+"F16.wireOp",EDGE,"E68.right"),sQuery(id+"F16.wireOp",EDGE,"E69"),sQuery(id+"F16.wireOp",EDGE,"E70"),sQuery(id+"F16.wireOp",EDGE,"E71"),sQuery(id+"F16.wireOp",EDGE,"E72"),sQuery(id+"F16.wireOp",EDGE,"E73.filletArc"),sQuery(id+"F16.wireOp",EDGE,"E74.filletArc"),sQuery(id+"F16.wireOp",EDGE,"E75.filletArc"),sQuery(id+"F16.wireOp",EDGE,"E76.filletArc"),sQuery(id+"F16.wireOp",EDGE,"E77"),sQuery(id+"F16.wireOp",EDGE,"E78.filletArc")])],"isStart":true});
            shell(context, id + "F18", {"entities" : qUnion([Q0]), "thickness" : 2 * mm});
        }
        {
            var Q0;
            Q0=qCreatedBy(makeId("Top.planeOp"),FACE);
            var sketch = newSketch(context, id + "F19", { "sketchPlane" : qUnion([Q0])});
            skLineSegment(sketch, "E79.bottom", {"start": v(136.83, 21.7) * mm, "end": v(142.83, 21.7) * mm});
            skLineSegment(sketch, "E79.top", {"start": v(136.83, -48.58) * mm, "end": v(142.83, -48.58) * mm});
            skLineSegment(sketch, "E79.left", {"start": v(136.83, 21.7) * mm, "end": v(136.83, -48.58) * mm});
            skLineSegment(sketch, "E79.right", {"start": v(142.83, 21.7) * mm, "end": v(142.83, -48.58) * mm});
            skLineSegment(sketch, "E80.bottom", {"start": v(337.83, 21.7) * mm, "end": v(343.83, 21.7) * mm});
            skLineSegment(sketch, "E80.top", {"start": v(337.83, -102.34) * mm, "end": v(343.83, -102.34) * mm});
            skLineSegment(sketch, "E80.left", {"start": v(337.83, 21.7) * mm, "end": v(337.83, -102.34) * mm});
            skLineSegment(sketch, "E80.right", {"start": v(343.83, 21.7) * mm, "end": v(343.83, -102.34) * mm});
            skCircle(sketch, "E81", {"center": v(139.83, 9.7) * mm, "radius": 1.5 * mm});
            skCircle(sketch, "E82", {"center": v(139.83, -38.58) * mm, "radius": 1.5 * mm});
            skCircle(sketch, "E83", {"center": v(340.83, 9.7) * mm, "radius": 1.5 * mm});
            skCircle(sketch, "E84", {"center": v(340.83, -42.3) * mm, "radius": 1.5 * mm});
            skCircle(sketch, "E85", {"center": v(340.83, -94.34) * mm, "radius": 1.5 * mm});
            skLineSegment(sketch, "E86.bottom", {"start": v(128.25, 8.7) * mm, "end": v(126.25, 8.7) * mm, "construction": true});
            skLineSegment(sketch, "E86.top", {"start": v(128.25, 10.7) * mm, "end": v(126.25, 10.7) * mm, "construction": true});
            skLineSegment(sketch, "E86.left", {"start": v(128.25, 8.7) * mm, "end": v(128.25, 10.7) * mm, "construction": true});
            skLineSegment(sketch, "E86.right", {"start": v(126.25, 8.7) * mm, "end": v(126.25, 10.7) * mm, "construction": true});
            skPoint(sketch, "E86.middle", {"position": v(127.25, 9.7) * mm});
            skLineSegment(sketch, "E87.bottom", {"start": v(128.25, -39.58) * mm, "end": v(126.25, -39.58) * mm});
            skLineSegment(sketch, "E87.top", {"start": v(128.25, -37.58) * mm, "end": v(126.25, -37.58) * mm});
            skLineSegment(sketch, "E87.left", {"start": v(128.25, -39.58) * mm, "end": v(128.25, -37.58) * mm});
            skLineSegment(sketch, "E87.right", {"start": v(126.25, -39.58) * mm, "end": v(126.25, -37.58) * mm});
            skPoint(sketch, "E87.middle", {"position": v(127.25, -38.58) * mm});
            skLineSegment(sketch, "E88.bottom", {"start": v(351.49, 8.7) * mm, "end": v(349.49, 8.7) * mm, "construction": true});
            skLineSegment(sketch, "E88.top", {"start": v(351.49, 10.7) * mm, "end": v(349.49, 10.7) * mm, "construction": true});
            skLineSegment(sketch, "E88.left", {"start": v(351.49, 8.7) * mm, "end": v(351.49, 10.7) * mm, "construction": true});
            skLineSegment(sketch, "E88.right", {"start": v(349.49, 8.7) * mm, "end": v(349.49, 10.7) * mm, "construction": true});
            skPoint(sketch, "E88.middle", {"position": v(350.49, 9.7) * mm});
            skLineSegment(sketch, "E89.bottom", {"start": v(351.49, -43.3) * mm, "end": v(349.49, -43.3) * mm, "construction": true});
            skLineSegment(sketch, "E89.top", {"start": v(351.49, -41.3) * mm, "end": v(349.49, -41.3) * mm, "construction": true});
            skLineSegment(sketch, "E89.left", {"start": v(351.49, -43.3) * mm, "end": v(351.49, -41.3) * mm, "construction": true});
            skLineSegment(sketch, "E89.right", {"start": v(349.49, -43.3) * mm, "end": v(349.49, -41.3) * mm, "construction": true});
            skPoint(sketch, "E89.middle", {"position": v(350.49, -42.3) * mm});
            skPoint(sketch, "E89.middle.positionSnap0", {"position": v(350.49, 8.7) * mm});
            skPoint(sketch, "E89.centerSnap0", {"position": v(350.49, 8.7) * mm});
            skLineSegment(sketch, "E90.bottom", {"start": v(351.49, -95.34) * mm, "end": v(349.49, -95.34) * mm, "construction": true});
            skLineSegment(sketch, "E90.top", {"start": v(351.49, -93.34) * mm, "end": v(349.49, -93.34) * mm, "construction": true});
            skLineSegment(sketch, "E90.left", {"start": v(351.49, -95.34) * mm, "end": v(351.49, -93.34) * mm, "construction": true});
            skLineSegment(sketch, "E90.right", {"start": v(349.49, -95.34) * mm, "end": v(349.49, -93.34) * mm, "construction": true});
            skPoint(sketch, "E90.middle", {"position": v(350.49, -94.34) * mm});
            skSolve(sketch);
        }
        {
            var Q0;
            Q0=makeQuery(id+"F17.opExtrude","CAP_FACE",FACE,{"disambiguationData":[OSD([sQuery(id+"F16.wireOp",EDGE,"E68.top"),sQuery(id+"F16.wireOp",EDGE,"E68.left"),sQuery(id+"F16.wireOp",EDGE,"E68.right"),sQuery(id+"F16.wireOp",EDGE,"E69"),sQuery(id+"F16.wireOp",EDGE,"E70"),sQuery(id+"F16.wireOp",EDGE,"E71"),sQuery(id+"F16.wireOp",EDGE,"E72"),sQuery(id+"F16.wireOp",EDGE,"E73.filletArc"),sQuery(id+"F16.wireOp",EDGE,"E74.filletArc"),sQuery(id+"F16.wireOp",EDGE,"E75.filletArc"),sQuery(id+"F16.wireOp",EDGE,"E76.filletArc"),sQuery(id+"F16.wireOp",EDGE,"E77"),sQuery(id+"F16.wireOp",EDGE,"E78.filletArc")])],"isStart":false});
            var sketch = newSketch(context, id + "F20", { "sketchPlane" : qUnion([Q0])});
            skLineSegment(sketch, "E91.bottom", {"start": v(149.83, 21.66) * mm, "end": v(330.83, 21.66) * mm});
            skLineSegment(sketch, "E91.top", {"start": v(185.06, -101.56) * mm, "end": v(330.83, -101.56) * mm});
            skLineSegment(sketch, "E91.left", {"start": v(149.83, 21.66) * mm, "end": v(149.83, -46.56) * mm});
            skLineSegment(sketch, "E91.right", {"start": v(330.83, 21.66) * mm, "end": v(330.83, -101.56) * mm});
            skLineSegment(sketch, "E92", {"start": v(149.83, -46.56) * mm, "end": v(185.06, -46.56) * mm});
            skLineSegment(sketch, "E93", {"start": v(185.06, -46.56) * mm, "end": v(185.06, -101.56) * mm});
            skCircle(sketch, "E94", {"center": v(168.08, 3.66) * mm, "radius": 7.25 * mm});
            skCircle(sketch, "E95", {"center": v(196.58, 3.66) * mm, "radius": 7.25 * mm});
            skCircle(sketch, "E96", {"center": v(225.08, 3.66) * mm, "radius": 7.25 * mm});
            skCircle(sketch, "E97", {"center": v(225.08, -29.34) * mm, "radius": 7.25 * mm});
            skCircle(sketch, "E98", {"center": v(238.33, -65.84) * mm, "radius": 5.5 * mm});
            skCircle(sketch, "E99", {"center": v(255.58, 3.66) * mm, "radius": 7.25 * mm});
            skCircle(sketch, "E100", {"center": v(255.58, -29.34) * mm, "radius": 7.25 * mm});
            skCircle(sketch, "E101", {"center": v(284.08, 3.66) * mm, "radius": 7.25 * mm});
            skCircle(sketch, "E102", {"center": v(312.58, 3.66) * mm, "radius": 7.25 * mm});
            skCircle(sketch, "E103", {"center": v(312.58, -29.34) * mm, "radius": 7.25 * mm});
            skCircle(sketch, "E104", {"center": v(312.58, -62.34) * mm, "radius": 7.25 * mm});
            skCircle(sketch, "E105", {"center": v(196.58, -29.34) * mm, "radius": 7.25 * mm});
            skCircle(sketch, "E106", {"center": v(312.58, -88.34) * mm, "radius": 7.25 * mm});
            skCircle(sketch, "E107", {"center": v(284.08, -29.34) * mm, "radius": 7.25 * mm});
            skLineSegment(sketch, "E108.top", {"start": v(210.33, 28.66) * mm, "end": v(270.33, 28.66) * mm});
            skLineSegment(sketch, "E108.left", {"start": v(210.33, 21.66) * mm, "end": v(210.33, 28.66) * mm});
            skLineSegment(sketch, "E108.right", {"start": v(270.33, 21.66) * mm, "end": v(270.33, 28.66) * mm});
            skLineSegment(sketch, "E109.left", {"start": v(260.83, -50.1) * mm, "end": v(260.83, -84.6) * mm});
            skLineSegment(sketch, "E109.right", {"start": v(279.33, -50.1) * mm, "end": v(279.33, -84.6) * mm});
            skArc(sketch, "E110", {"start": v(260.83, -84.6) * mm, "mid": v(270.08, -93.84) * mm, "end": v(279.33, -84.6) * mm});
            skLineSegment(sketch, "E111", {"start": v(260.83, -50.1) * mm, "end": v(279.33, -50.1) * mm});
            skCircle(sketch, "E112", {"center": v(168.08, -28.15) * mm, "radius": 4 * mm});
            skCircle(sketch, "E113", {"center": v(240.33, 16.66) * mm, "radius": 4 * mm});
            skCircle(sketch, "E114", {"center": v(293.83, -60.3) * mm, "radius": 4 * mm});
            skLineSegment(sketch, "E115.bottom", {"start": v(149.83, 21.66) * mm, "end": v(148.83, 21.66) * mm});
            skLineSegment(sketch, "E115.top", {"start": v(149.83, -46.56) * mm, "end": v(146.83, -46.56) * mm});
            skLineSegment(sketch, "E115.right", {"start": v(146.83, 19.66) * mm, "end": v(146.83, -46.56) * mm});
            skLineSegment(sketch, "E116.bottom", {"start": v(146.83, -46.56) * mm, "end": v(185.06, -46.56) * mm});
            skLineSegment(sketch, "E116.top", {"start": v(148.83, -49.56) * mm, "end": v(185.06, -49.56) * mm});
            skLineSegment(sketch, "E116.left", {"start": v(146.83, -46.56) * mm, "end": v(146.83, -47.56) * mm});
            skLineSegment(sketch, "E116.right", {"start": v(185.06, -46.56) * mm, "end": v(185.06, -49.56) * mm});
            skLineSegment(sketch, "E117.bottom", {"start": v(185.06, -101.56) * mm, "end": v(182.06, -101.56) * mm});
            skLineSegment(sketch, "E117.top", {"start": v(185.06, -49.56) * mm, "end": v(182.06, -49.56) * mm});
            skLineSegment(sketch, "E117.left", {"start": v(185.06, -101.56) * mm, "end": v(185.06, -49.56) * mm});
            skLineSegment(sketch, "E117.right", {"start": v(182.06, -101.56) * mm, "end": v(182.06, -49.56) * mm});
            skLineSegment(sketch, "E118.bottom", {"start": v(182.06, -101.56) * mm, "end": v(254.06, -101.56) * mm});
            skLineSegment(sketch, "E118.top", {"start": v(182.06, -104.56) * mm, "end": v(254.06, -104.56) * mm});
            skLineSegment(sketch, "E118.left", {"start": v(182.06, -101.56) * mm, "end": v(182.06, -104.56) * mm});
            skLineSegment(sketch, "E118.right", {"start": v(254.06, -101.56) * mm, "end": v(254.06, -104.56) * mm});
            skLineSegment(sketch, "E119.bottom", {"start": v(269.83, -101.56) * mm, "end": v(305.83, -101.56) * mm});
            skLineSegment(sketch, "E119.top", {"start": v(269.83, -104.56) * mm, "end": v(305.83, -104.56) * mm});
            skLineSegment(sketch, "E119.left", {"start": v(269.83, -101.56) * mm, "end": v(269.83, -104.56) * mm});
            skLineSegment(sketch, "E119.right", {"start": v(305.83, -101.56) * mm, "end": v(305.83, -104.56) * mm});
            skLineSegment(sketch, "E120.bottom", {"start": v(330.83, 21.66) * mm, "end": v(331.83, 21.66) * mm});
            skLineSegment(sketch, "E120.top", {"start": v(330.83, -101.56) * mm, "end": v(333.83, -101.56) * mm});
            skLineSegment(sketch, "E120.right", {"start": v(333.83, 19.66) * mm, "end": v(333.83, -101.56) * mm});
            skLineSegment(sketch, "E121.bottom", {"start": v(320.83, -101.56) * mm, "end": v(333.83, -101.56) * mm});
            skLineSegment(sketch, "E121.top", {"start": v(320.83, -104.56) * mm, "end": v(333.83, -104.56) * mm});
            skLineSegment(sketch, "E121.left", {"start": v(320.83, -101.56) * mm, "end": v(320.83, -104.56) * mm});
            skLineSegment(sketch, "E121.right", {"start": v(333.83, -101.56) * mm, "end": v(333.83, -104.56) * mm});
            skLineSegment(sketch, "E122.bottom", {"start": v(210.33, 28.66) * mm, "end": v(209.33, 28.66) * mm});
            skLineSegment(sketch, "E122.top", {"start": v(210.33, 21.66) * mm, "end": v(209.33, 21.66) * mm});
            skLineSegment(sketch, "E122.left", {"start": v(210.33, 28.66) * mm, "end": v(210.33, 21.66) * mm});
            skLineSegment(sketch, "E122.right", {"start": v(209.33, 28.66) * mm, "end": v(209.33, 21.66) * mm});
            skLineSegment(sketch, "E123.bottom", {"start": v(209.33, 21.66) * mm, "end": v(203.33, 21.66) * mm});
            skLineSegment(sketch, "E123.top", {"start": v(209.33, 22.66) * mm, "end": v(203.33, 22.66) * mm});
            skLineSegment(sketch, "E123.left", {"start": v(209.33, 21.66) * mm, "end": v(209.33, 22.66) * mm});
            skLineSegment(sketch, "E123.right", {"start": v(203.33, 21.66) * mm, "end": v(203.33, 22.66) * mm});
            skLineSegment(sketch, "E124.bottom", {"start": v(270.33, 28.66) * mm, "end": v(271.33, 28.66) * mm});
            skLineSegment(sketch, "E124.top", {"start": v(270.33, 21.66) * mm, "end": v(271.33, 21.66) * mm});
            skLineSegment(sketch, "E124.left", {"start": v(270.33, 28.66) * mm, "end": v(270.33, 21.66) * mm});
            skLineSegment(sketch, "E124.right", {"start": v(271.33, 28.66) * mm, "end": v(271.33, 21.66) * mm});
            skLineSegment(sketch, "E125.bottom", {"start": v(271.33, 21.66) * mm, "end": v(277.33, 21.66) * mm});
            skLineSegment(sketch, "E125.top", {"start": v(271.33, 22.66) * mm, "end": v(277.33, 22.66) * mm});
            skLineSegment(sketch, "E125.left", {"start": v(271.33, 21.66) * mm, "end": v(271.33, 22.66) * mm});
            skLineSegment(sketch, "E125.right", {"start": v(277.33, 21.66) * mm, "end": v(277.33, 22.66) * mm});
            skPoint(sketch, "E126.visualSharp", {"position": v(146.83, 21.66) * mm});
            skArc(sketch, "E126.filletArc", {"start": v(148.83, 21.66) * mm, "mid": v(147.42, 21.07) * mm, "end": v(146.83, 19.66) * mm});
            skPoint(sketch, "E127.visualSharp", {"position": v(333.83, 21.66) * mm});
            skArc(sketch, "E127.filletArc", {"start": v(333.83, 19.66) * mm, "mid": v(333.25, 21.07) * mm, "end": v(331.83, 21.66) * mm});
            skPoint(sketch, "E128.visualSharp", {"position": v(146.83, -49.56) * mm});
            skArc(sketch, "E128.filletArc", {"start": v(146.83, -47.56) * mm, "mid": v(147.42, -48.97) * mm, "end": v(148.83, -49.56) * mm});
            skCircle(sketch, "E129", {"center": v(152.58, 13.66) * mm, "radius": 1.5 * mm, "construction": true});
            skCircle(sketch, "E130", {"center": v(152.58, -9.34) * mm, "radius": 1.5 * mm, "construction": true});
            skLineSegment(sketch, "E131.bottom", {"start": v(155.33, 16.16) * mm, "end": v(160.33, 16.16) * mm, "construction": true});
            skLineSegment(sketch, "E131.top", {"start": v(155.33, -8.84) * mm, "end": v(160.33, -8.84) * mm, "construction": true});
            skLineSegment(sketch, "E131.left", {"start": v(155.33, 16.16) * mm, "end": v(155.33, -8.84) * mm, "construction": true});
            skLineSegment(sketch, "E131.right", {"start": v(160.33, 16.16) * mm, "end": v(160.33, -8.84) * mm, "construction": true});
            skCircle(sketch, "E132", {"center": v(157.83, 11.16) * mm, "radius": 1 * mm, "construction": true});
            skPoint(sketch, "E132.centerSnap0", {"position": v(157.83, 16.16) * mm});
            skCircle(sketch, "E133", {"center": v(157.83, -3.84) * mm, "radius": 1 * mm, "construction": true});
            skCircle(sketch, "E134", {"center": v(152.58, -34.34) * mm, "radius": 1.5 * mm, "construction": true});
            skLineSegment(sketch, "E135.bottom", {"start": v(320.33, 16.16) * mm, "end": v(325.33, 16.16) * mm, "construction": true});
            skLineSegment(sketch, "E135.top", {"start": v(320.33, -8.84) * mm, "end": v(325.33, -8.84) * mm, "construction": true});
            skLineSegment(sketch, "E135.left", {"start": v(320.33, 16.16) * mm, "end": v(320.33, -8.84) * mm, "construction": true});
            skLineSegment(sketch, "E135.right", {"start": v(325.33, 16.16) * mm, "end": v(325.33, -8.84) * mm, "construction": true});
            skCircle(sketch, "E136", {"center": v(322.83, 11.16) * mm, "radius": 1 * mm});
            skPoint(sketch, "E136.centerSnap0", {"position": v(322.83, 16.16) * mm});
            skCircle(sketch, "E137", {"center": v(322.83, -3.84) * mm, "radius": 1 * mm});
            skLineSegment(sketch, "E138", {"start": v(326.4, -29.34) * mm, "end": v(181.1, -29.34) * mm, "construction": true});
            skLineSegment(sketch, "E139", {"start": v(157.98, 3.66) * mm, "end": v(328.03, 3.66) * mm, "construction": true});
            skCircle(sketch, "E140", {"center": v(238.33, -65.84) * mm, "radius": 12.5 * mm, "construction": true});
            skSolve(sketch);
        }
        {
            var Q0;
            Q0=makeQuery(id+"F20.imprint","IMPRINT",FACE,{"disambiguationData":[TD([[makeQuery(id+"F20.imprint","IMPRINT",EDGE,{"derivedFrom":sQuery(id+"F20.wireOp",EDGE,"E94")}),1.0]])]});
            var Q1;
            Q1=makeQuery(id+"F20.imprint","IMPRINT",FACE,{"disambiguationData":[TD([[makeQuery(id+"F20.imprint","IMPRINT",EDGE,{"derivedFrom":sQuery(id+"F20.wireOp",EDGE,"E95")}),1.0]])]});
            var Q2;
            Q2=makeQuery(id+"F20.imprint","IMPRINT",FACE,{"disambiguationData":[TD([[makeQuery(id+"F20.imprint","IMPRINT",EDGE,{"derivedFrom":sQuery(id+"F20.wireOp",EDGE,"E96")}),1.0]])]});
            var Q3;
            Q3=makeQuery(id+"F20.imprint","IMPRINT",FACE,{"disambiguationData":[TD([[makeQuery(id+"F20.imprint","IMPRINT",EDGE,{"derivedFrom":sQuery(id+"F20.wireOp",EDGE,"E99")}),1.0]])]});
            var Q4;
            Q4=makeQuery(id+"F20.imprint","IMPRINT",FACE,{"disambiguationData":[TD([[makeQuery(id+"F20.imprint","IMPRINT",EDGE,{"derivedFrom":sQuery(id+"F20.wireOp",EDGE,"E101")}),1.0]])]});
            var Q5;
            Q5=makeQuery(id+"F20.imprint","IMPRINT",FACE,{"disambiguationData":[TD([[makeQuery(id+"F20.imprint","IMPRINT",EDGE,{"derivedFrom":sQuery(id+"F20.wireOp",EDGE,"E102")}),1.0]])]});
            var Q6;
            Q6=makeQuery(id+"F20.imprint","IMPRINT",FACE,{"disambiguationData":[TD([[makeQuery(id+"F20.imprint","IMPRINT",EDGE,{"derivedFrom":sQuery(id+"F20.wireOp",EDGE,"E105")}),1.0]])]});
            var Q7;
            Q7=makeQuery(id+"F20.imprint","IMPRINT",FACE,{"disambiguationData":[TD([[makeQuery(id+"F20.imprint","IMPRINT",EDGE,{"derivedFrom":sQuery(id+"F20.wireOp",EDGE,"E97")}),1.0]])]});
            var Q8;
            Q8=makeQuery(id+"F20.imprint","IMPRINT",FACE,{"disambiguationData":[TD([[makeQuery(id+"F20.imprint","IMPRINT",EDGE,{"derivedFrom":sQuery(id+"F20.wireOp",EDGE,"E100")}),1.0]])]});
            var Q9;
            Q9=makeQuery(id+"F20.imprint","IMPRINT",FACE,{"disambiguationData":[TD([[makeQuery(id+"F20.imprint","IMPRINT",EDGE,{"derivedFrom":sQuery(id+"F20.wireOp",EDGE,"E107")}),1.0]])]});
            var Q10;
            Q10=makeQuery(id+"F20.imprint","IMPRINT",FACE,{"disambiguationData":[TD([[makeQuery(id+"F20.imprint","IMPRINT",EDGE,{"derivedFrom":sQuery(id+"F20.wireOp",EDGE,"E103")}),1.0]])]});
            var Q11;
            Q11=makeQuery(id+"F20.imprint","IMPRINT",FACE,{"disambiguationData":[TD([[makeQuery(id+"F20.imprint","IMPRINT",EDGE,{"derivedFrom":sQuery(id+"F20.wireOp",EDGE,"E109.left")}),1.0]])]});
            var Q12;
            Q12=makeQuery(id+"F20.imprint","IMPRINT",FACE,{"disambiguationData":[TD([[makeQuery(id+"F20.imprint","IMPRINT",EDGE,{"derivedFrom":sQuery(id+"F20.wireOp",EDGE,"E104")}),1.0]])]});
            var Q13;
            Q13=makeQuery(id+"F20.imprint","IMPRINT",FACE,{"disambiguationData":[TD([[makeQuery(id+"F20.imprint","IMPRINT",EDGE,{"derivedFrom":sQuery(id+"F20.wireOp",EDGE,"E106")}),1.0]])]});
            var Q14;
            Q14=makeQuery(id+"F20.imprint","IMPRINT",FACE,{"disambiguationData":[TD([[makeQuery(id+"F20.imprint","IMPRINT",EDGE,{"derivedFrom":sQuery(id+"F20.wireOp",EDGE,"E98")}),1.0]])]});
            var Q15;
            Q15=makeQuery(id+"F20.imprint","IMPRINT",FACE,{"disambiguationData":[TD([[makeQuery(id+"F20.imprint","IMPRINT",EDGE,{"derivedFrom":sQuery(id+"F20.wireOp",EDGE,"E114")}),1.0]])]});
            var Q16;
            Q16=makeQuery(id+"F20.imprint","IMPRINT",FACE,{"disambiguationData":[TD([[makeQuery(id+"F20.imprint","IMPRINT",EDGE,{"derivedFrom":sQuery(id+"F20.wireOp",EDGE,"E112")}),1.0]])]});
            var Q17;
            Q17=makeQuery(id+"F20.imprint","IMPRINT",FACE,{"disambiguationData":[TD([[makeQuery(id+"F20.imprint","IMPRINT",EDGE,{"derivedFrom":sQuery(id+"F20.wireOp",EDGE,"E113")}),1.0]])]});
            extrude(context, id + "F21", {"entities" : qUnion([Q0, Q1, Q2, Q3, Q4, Q5, Q6, Q7, Q8, Q9, Q10, Q11, Q12, Q13, Q14, Q15, Q16, Q17]), "operationType" : NewBodyOperationType.REMOVE, "oppositeDirection" : true, "depth" : 5 * mm});
        }
        {
            var Q0;
            Q0=qCreatedBy(makeId("Top.planeOp"),FACE);
            var sketch = newSketch(context, id + "F22", { "sketchPlane" : qUnion([Q0])});
            skLineSegment(sketch, "E141.bottom", {"start": v(87.15, 21.4) * mm, "end": v(104.65, 21.4) * mm});
            skLineSegment(sketch, "E141.top", {"start": v(87.15, -48.87) * mm, "end": v(104.65, -48.87) * mm});
            skLineSegment(sketch, "E141.left", {"start": v(87.15, 21.4) * mm, "end": v(87.15, -48.87) * mm});
            skLineSegment(sketch, "E141.right", {"start": v(104.65, 21.4) * mm, "end": v(104.65, -48.87) * mm});
            skCircle(sketch, "E142", {"center": v(102.15, 16.4) * mm, "radius": 1 * mm, "construction": true});
            skCircle(sketch, "E143", {"center": v(102.65, 13.4) * mm, "radius": 1.1 * mm});
            skCircle(sketch, "E144", {"center": v(102.65, -9.6) * mm, "radius": 1.1 * mm});
            skCircle(sketch, "E145", {"center": v(102.65, -34.6) * mm, "radius": 1.1 * mm});
            skCircle(sketch, "E146", {"center": v(90.9, 9.4) * mm, "radius": 1.5 * mm});
            skCircle(sketch, "E147", {"center": v(90.9, -38.87) * mm, "radius": 1.5 * mm});
            skSolve(sketch);
        }
        {
            var Q0;
            Q0=makeQuery(id+"F22.imprint","IMPRINT",FACE,{"disambiguationData":[TD([[makeQuery(id+"F22.imprint","IMPRINT",EDGE,{"derivedFrom":sQuery(id+"F22.wireOp",EDGE,"E141.bottom")}),-1.0]])]});
            extrude(context, id + "F23", {"entities" : qUnion([Q0]), "depth" : 1 * mm});
        }
        {
            var Q0;
            Q0=qCreatedBy(makeId("Top.planeOp"),FACE);
            var sketch = newSketch(context, id + "F24", { "sketchPlane" : qUnion([Q0])});
            skLineSegment(sketch, "E148.bottom", {"start": v(370, 20.23) * mm, "end": v(387.5, 20.23) * mm});
            skLineSegment(sketch, "E148.top", {"start": v(370, -107.8) * mm, "end": v(387.5, -107.8) * mm});
            skLineSegment(sketch, "E148.left", {"start": v(370, 20.23) * mm, "end": v(370, -107.8) * mm});
            skLineSegment(sketch, "E148.right", {"start": v(387.5, 20.23) * mm, "end": v(387.5, -107.8) * mm});
            skCircle(sketch, "E149", {"center": v(372, 12.23) * mm, "radius": 1.1 * mm});
            skCircle(sketch, "E150", {"center": v(372, -7.77) * mm, "radius": 1.1 * mm});
            skCircle(sketch, "E151", {"center": v(372, -27.77) * mm, "radius": 1.1 * mm});
            skCircle(sketch, "E152", {"center": v(372, -47.77) * mm, "radius": 1.1 * mm});
            skCircle(sketch, "E153", {"center": v(372, -67.77) * mm, "radius": 1.1 * mm});
            skCircle(sketch, "E154", {"center": v(372, -87.77) * mm, "radius": 1.1 * mm});
            skCircle(sketch, "E155", {"center": v(383.74, 8.23) * mm, "radius": 1.5 * mm});
            skCircle(sketch, "E156", {"center": v(383.74, -43.77) * mm, "radius": 1.5 * mm});
            skCircle(sketch, "E157", {"center": v(383.74, -95.8) * mm, "radius": 1.5 * mm});
            skSolve(sketch);
        }
        {
            var Q0;
            Q0=makeQuery(id+"F24.imprint","IMPRINT",FACE,{"disambiguationData":[TD([[makeQuery(id+"F24.imprint","IMPRINT",EDGE,{"derivedFrom":sQuery(id+"F24.wireOp",EDGE,"E148.bottom")}),-1.0]])]});
            extrude(context, id + "F25", {"entities" : qUnion([Q0]), "depth" : 1 * mm});
        }
        {
            var Q0;
            Q0=makeQuery(id+"FwYwuyrlYUuTAHt_4.boolean.opBoolean","MERGE",FACE,{"derivedFrom":[makeQuery(id+"F17.opExtrude","CAP_FACE",FACE,{"disambiguationData":[OSD([sQuery(id+"F16.wireOp",EDGE,"E68.top"),sQuery(id+"F16.wireOp",EDGE,"E68.left"),sQuery(id+"F16.wireOp",EDGE,"E68.right"),sQuery(id+"F16.wireOp",EDGE,"E69"),sQuery(id+"F16.wireOp",EDGE,"E70"),sQuery(id+"F16.wireOp",EDGE,"E71"),sQuery(id+"F16.wireOp",EDGE,"E72"),sQuery(id+"F16.wireOp",EDGE,"E73.filletArc"),sQuery(id+"F16.wireOp",EDGE,"E74.filletArc"),sQuery(id+"F16.wireOp",EDGE,"E75.filletArc"),sQuery(id+"F16.wireOp",EDGE,"E76.filletArc"),sQuery(id+"F16.wireOp",EDGE,"E77"),sQuery(id+"F16.wireOp",EDGE,"E78.filletArc")])],"isStart":true}),makeQuery(id+"FwYwuyrlYUuTAHt_4.opExtrude","CAP_FACE",FACE,{"disambiguationData":[OSD([sQuery(id+"F19.wireOp",EDGE,"E79.bottom"),sQuery(id+"F19.wireOp",EDGE,"E79.top"),sQuery(id+"F19.wireOp",EDGE,"E79.left"),sQuery(id+"F19.wireOp",EDGE,"E79.right"),sQuery(id+"F19.wireOp",EDGE,"E81"),sQuery(id+"F19.wireOp",EDGE,"E82")])],"isStart":true}),makeQuery(id+"FwYwuyrlYUuTAHt_4.opExtrude","CAP_FACE",FACE,{"disambiguationData":[OSD([sQuery(id+"F19.wireOp",EDGE,"E80.bottom"),sQuery(id+"F19.wireOp",EDGE,"E80.top"),sQuery(id+"F19.wireOp",EDGE,"E80.left"),sQuery(id+"F19.wireOp",EDGE,"E80.right"),sQuery(id+"F19.wireOp",EDGE,"E83"),sQuery(id+"F19.wireOp",EDGE,"E84"),sQuery(id+"F19.wireOp",EDGE,"E85")])],"isStart":true})]});
            extrude(context, id + "F26", {"entities" : qUnion([Q0]), "operationType" : NewBodyOperationType.ADD, "depth" : 2 * mm});
        }
        {
            var Q0;
            Q0=makeQuery(id+"F26.opExtrude","CAP_FACE",FACE,{"disambiguationData":[OSD([sQuery(id+"F16.wireOp",EDGE,"E68.top"),sQuery(id+"F16.wireOp",EDGE,"E68.left"),sQuery(id+"F16.wireOp",EDGE,"E68.right"),sQuery(id+"F16.wireOp",EDGE,"E69"),sQuery(id+"F16.wireOp",EDGE,"E70"),sQuery(id+"F16.wireOp",EDGE,"E71"),sQuery(id+"F16.wireOp",EDGE,"E72"),sQuery(id+"F16.wireOp",EDGE,"E73.filletArc"),sQuery(id+"F16.wireOp",EDGE,"E74.filletArc"),sQuery(id+"F16.wireOp",EDGE,"E75.filletArc"),sQuery(id+"F16.wireOp",EDGE,"E76.filletArc"),sQuery(id+"F16.wireOp",EDGE,"E77"),sQuery(id+"F16.wireOp",EDGE,"E78.filletArc"),sQuery(id+"F19.wireOp",EDGE,"E79.bottom"),sQuery(id+"F19.wireOp",EDGE,"E79.top"),sQuery(id+"F19.wireOp",EDGE,"E79.left"),sQuery(id+"F19.wireOp",EDGE,"E79.right"),sQuery(id+"F19.wireOp",EDGE,"E80.bottom"),sQuery(id+"F19.wireOp",EDGE,"E80.top"),sQuery(id+"F19.wireOp",EDGE,"E80.left"),sQuery(id+"F19.wireOp",EDGE,"E80.right"),sQuery(id+"F19.wireOp",EDGE,"E81"),sQuery(id+"F19.wireOp",EDGE,"E82"),sQuery(id+"F19.wireOp",EDGE,"E83"),sQuery(id+"F19.wireOp",EDGE,"E84"),sQuery(id+"F19.wireOp",EDGE,"E85")])],"isStart":false});
            var sketch = newSketch(context, id + "F27", { "sketchPlane" : qUnion([Q0])});
            skLineSegment(sketch, "E158.bottom", {"start": v(353.41, -21.7) * mm, "end": v(120.72, -21.7) * mm});
            skLineSegment(sketch, "E158.top", {"start": v(353.41, 48.58) * mm, "end": v(120.72, 48.58) * mm});
            skLineSegment(sketch, "E158.left", {"start": v(353.41, -21.7) * mm, "end": v(353.41, 48.58) * mm});
            skLineSegment(sketch, "E158.right", {"start": v(120.72, -21.7) * mm, "end": v(120.72, 48.58) * mm});
            skLineSegment(sketch, "E159.top", {"start": v(353.41, 106.34) * mm, "end": v(173.9, 106.34) * mm});
            skLineSegment(sketch, "E159.left", {"start": v(353.41, 48.58) * mm, "end": v(353.41, 106.34) * mm});
            skLineSegment(sketch, "E160", {"start": v(142.83, 48.58) * mm, "end": v(161.72, 60.75) * mm});
            skLineSegment(sketch, "E161", {"start": v(161.72, 60.75) * mm, "end": v(173.9, 93.58) * mm});
            skLineSegment(sketch, "E162", {"start": v(173.9, 93.58) * mm, "end": v(173.9, 106.34) * mm});
            skPoint(sketch, "E159.right.end.orphan", {"position": v(120.72, 106.34) * mm});
            skSolve(sketch);
        }
        {
            var Q0;
            Q0=qSketchRegion(id+"F27",true);
            extrude(context, id + "F28", {"entities" : qUnion([Q0]), "operationType" : NewBodyOperationType.REMOVE, "oppositeDirection" : true, "depth" : 2 * mm});
        }
        {
            var Q0;
            Q0=makeQuery(id+"F20.imprint","IMPRINT",FACE,{"disambiguationData":[TD([[makeQuery(id+"F20.imprint","IMPRINT",EDGE,{"derivedFrom":sQuery(id+"F20.wireOp",EDGE,"E108.top")}),1.0]])]});
            var sketch = newSketch(context, id + "F29", { "sketchPlane" : qUnion([Q0])});
            skLineSegment(sketch, "E163.bottom", {"start": v(150.36, 18.45) * mm, "end": v(329.5, 18.45) * mm});
            skLineSegment(sketch, "E163.top", {"start": v(178.72, -100.9) * mm, "end": v(329.5, -100.9) * mm});
            skLineSegment(sketch, "E163.left", {"start": v(150.36, 18.45) * mm, "end": v(150.36, -49.22) * mm});
            skLineSegment(sketch, "E163.right", {"start": v(329.5, 18.45) * mm, "end": v(329.5, -100.9) * mm});
            skLineSegment(sketch, "E164", {"start": v(150.36, -49.22) * mm, "end": v(178.72, -49.22) * mm});
            skLineSegment(sketch, "E165", {"start": v(178.72, -49.22) * mm, "end": v(178.72, -100.9) * mm});
            skLineSegment(sketch, "E166.bottom", {"start": v(8.56, -7.76) * mm, "end": v(28.56, -7.76) * mm});
            skLineSegment(sketch, "E166.top", {"start": v(8.56, -27.76) * mm, "end": v(28.56, -27.76) * mm});
            skLineSegment(sketch, "E166.left", {"start": v(8.56, -7.76) * mm, "end": v(8.56, -27.76) * mm});
            skLineSegment(sketch, "E166.right", {"start": v(28.56, -7.76) * mm, "end": v(28.56, -27.76) * mm});
            skCircle(sketch, "E167", {"center": v(18.56, -17.76) * mm, "radius": 7.5 * mm});
            skPoint(sketch, "E167.centerSnap0", {"position": v(8.56, -17.76) * mm});
            skPoint(sketch, "E167.centerSnap1", {"position": v(18.56, -7.76) * mm});
            skLineSegment(sketch, "E168.left", {"start": v(-58.94, -27.5) * mm, "end": v(-58.94, -58.75) * mm});
            skLineSegment(sketch, "E168.right", {"start": v(-39.94, -27.5) * mm, "end": v(-39.94, -58.75) * mm});
            skArc(sketch, "E169", {"start": v(-58.94, -58.75) * mm, "mid": v(-49.44, -68.25) * mm, "end": v(-39.94, -58.75) * mm});
            skLineSegment(sketch, "E170", {"start": v(-58.94, -27.5) * mm, "end": v(-39.94, -27.5) * mm});
            skLineSegment(sketch, "E171.bottom", {"start": v(-61.94, -24.5) * mm, "end": v(-36.94, -24.5) * mm});
            skLineSegment(sketch, "E171.top", {"start": v(-61.94, -71.25) * mm, "end": v(-36.94, -71.25) * mm});
            skLineSegment(sketch, "E171.left", {"start": v(-61.94, -24.5) * mm, "end": v(-61.94, -71.25) * mm});
            skLineSegment(sketch, "E171.right", {"start": v(-36.94, -24.5) * mm, "end": v(-36.94, -71.25) * mm});
            skSolve(sketch);
        }
        {
            var Q0;
            Q0=makeQuery(id+"F29.imprint","IMPRINT",FACE,{"disambiguationData":[TD([[makeQuery(id+"F29.imprint","IMPRINT",EDGE,{"derivedFrom":sQuery(id+"F29.wireOp",EDGE,"E166.bottom")}),-1.0]])]});
            var Q1;
            Q1=makeQuery(id+"F29.imprint","IMPRINT",FACE,{"disambiguationData":[TD([[makeQuery(id+"F29.imprint","IMPRINT",EDGE,{"derivedFrom":sQuery(id+"F29.wireOp",EDGE,"E168.left")}),-1.0]])]});
            extrude(context, id + "F30", {"entities" : qUnion([Q0, Q1]), "depth" : 2 * mm});
        }
        {
            var Q0;
            Q0=makeQuery(id+"F25.opExtrude","SWEPT_FACE",FACE,{"disambiguationData":[OSD([sQuery(id+"F24.wireOp",EDGE,"E148.left")])]});
            extrude(context, id + "F31", {"entities" : qUnion([Q0]), "operationType" : NewBodyOperationType.ADD, "depth" : 1 * mm});
        }
        {
            var Q0;
            Q0=makeQuery(id+"F23.opExtrude","SWEPT_FACE",FACE,{"disambiguationData":[OSD([sQuery(id+"F22.wireOp",EDGE,"E141.right")])]});
            extrude(context, id + "F32", {"entities" : qUnion([Q0]), "operationType" : NewBodyOperationType.ADD, "depth" : 1 * mm});
        }
        {
            var Q0;
            Q0=makeQuery(id+"F25.opExtrude","SWEPT_EDGE",EDGE,{"disambiguationData":[OSD([sQuery(id+"F24.wireOp",EDGE,"E148.bottom"),sQuery(id+"F24.wireOp",EDGE,"E148.right")])]});
            var Q1;
            Q1=makeQuery(id+"F31.opExtrude","CAP_EDGE",EDGE,{"disambiguationData":[OSD([sQuery(id+"F24.wireOp",EDGE,"E148.bottom"),sQuery(id+"F24.wireOp",EDGE,"E148.left")])],"isStart":false});
            var Q2;
            Q2=makeQuery(id+"F25.opExtrude","SWEPT_EDGE",EDGE,{"disambiguationData":[OSD([sQuery(id+"F24.wireOp",EDGE,"E148.top"),sQuery(id+"F24.wireOp",EDGE,"E148.right")])]});
            var Q3;
            Q3=makeQuery(id+"F31.opExtrude","CAP_EDGE",EDGE,{"disambiguationData":[OSD([sQuery(id+"F24.wireOp",EDGE,"E148.top"),sQuery(id+"F24.wireOp",EDGE,"E148.left")])],"isStart":false});
            var Q4;
            Q4=makeQuery(id+"F32.opExtrude","CAP_EDGE",EDGE,{"disambiguationData":[OSD([sQuery(id+"F22.wireOp",EDGE,"E141.top"),sQuery(id+"F22.wireOp",EDGE,"E141.right")])],"isStart":false});
            var Q5;
            Q5=makeQuery(id+"F23.opExtrude","SWEPT_EDGE",EDGE,{"disambiguationData":[OSD([sQuery(id+"F22.wireOp",EDGE,"E141.top"),sQuery(id+"F22.wireOp",EDGE,"E141.left")])]});
            var Q6;
            Q6=makeQuery(id+"F32.opExtrude","CAP_EDGE",EDGE,{"disambiguationData":[OSD([sQuery(id+"F22.wireOp",EDGE,"E141.bottom"),sQuery(id+"F22.wireOp",EDGE,"E141.right")])],"isStart":false});
            var Q7;
            Q7=makeQuery(id+"F23.opExtrude","SWEPT_EDGE",EDGE,{"disambiguationData":[OSD([sQuery(id+"F22.wireOp",EDGE,"E141.bottom"),sQuery(id+"F22.wireOp",EDGE,"E141.left")])]});
            fillet(context, id + "F33", {"entities" : qUnion([Q0, Q1, Q2, Q3, Q4, Q5, Q6, Q7]), "radius" : 2 * mm, "tangentPropagation" : true, "allowEdgeOverflow" : false});
        }
    });
